# Revit family: Accessory-Remote_Puck-KOHLER-Parallel-K-29341T
name_source: partatom
category: Specialty Equipment
units: mm (PartAtom-declared; Revit-internal decimal feet)

## family parameters
Cut with Voids When Loaded = No
Host = Face
OmniClass Number = 23.31.25.00
OmniClass Title = Toilet and Bath Specialties
Part Type = Normal
Room Calculation Point = No
Round Connector Dimension = Use Diameter
Shared = No

## types (1)
- 7-Black Black
    ADA Compliant = No
    Assembly Code = C1030200
    Date Modified = 10/20/2023
    Default Elevation = 42"
    Description = Remote Puck
    Finish = Kohler-Plastic-7-Black_Black
    Height = 2 9/16"
    Length = 15/16"
    Manufacturer = Kohler Co.
    Master Format 2014 = 10 28 00
    Master Format 2014 Name = Toilet, Bath, and Laundry Accessories
    Material = Plastic
    Model = K-29341T-7
    Product Name = Parallel
    Type = 1
    URL = http://www.kohler.com.cn
    WaterSense Certified = No
    Width = 2 9/16"

## geometry (parser evidence)
native form markers: Sweep x5
no freeform markers — native parametric forms only
